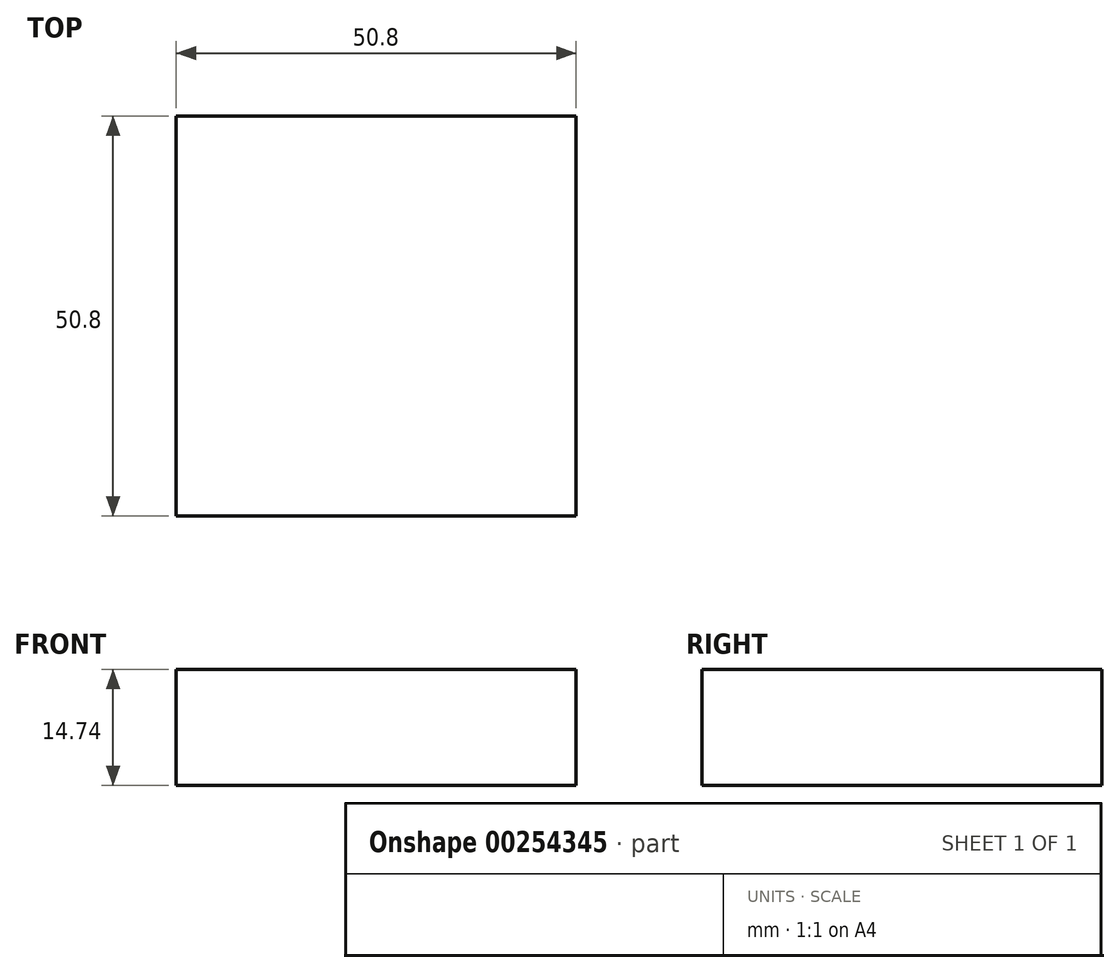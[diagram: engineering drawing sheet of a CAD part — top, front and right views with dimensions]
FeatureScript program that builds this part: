
annotation { "Feature Type Name" : "Feature", "Feature Type Description" : "" }
export const myFeature = defineFeature(function(context is Context, id is Id, definition is map)
    precondition{}
    {
        {
            var Q0;
            Q0=qCreatedBy(makeId("Front.planeOp"),FACE);
            var sketch = newSketch(context, id + "F0", { "sketchPlane" : qUnion([Q0])});
            skLineSegment(sketch, "E0.bottom", {"start": v(25.4, -7.37) * mm, "end": v(-25.4, -7.37) * mm});
            skLineSegment(sketch, "E0.top", {"start": v(25.4, 7.37) * mm, "end": v(-25.4, 7.37) * mm});
            skLineSegment(sketch, "E0.left", {"start": v(25.4, -7.37) * mm, "end": v(25.4, 7.37) * mm});
            skLineSegment(sketch, "E0.right", {"start": v(-25.4, -7.37) * mm, "end": v(-25.4, 7.37) * mm});
            skPoint(sketch, "E0.middle", {"position": v(0, 0) * mm});
            skSolve(sketch);
        }
        {
            var Q0;
            Q0 = qSketchRegion(id + "F0", true);
            extrude(context, id + "F1", {"entities" : qUnion([Q0]), "endBound" : BoundingType.SYMMETRIC, "depth" : 50.8 * mm});
        }
    });
